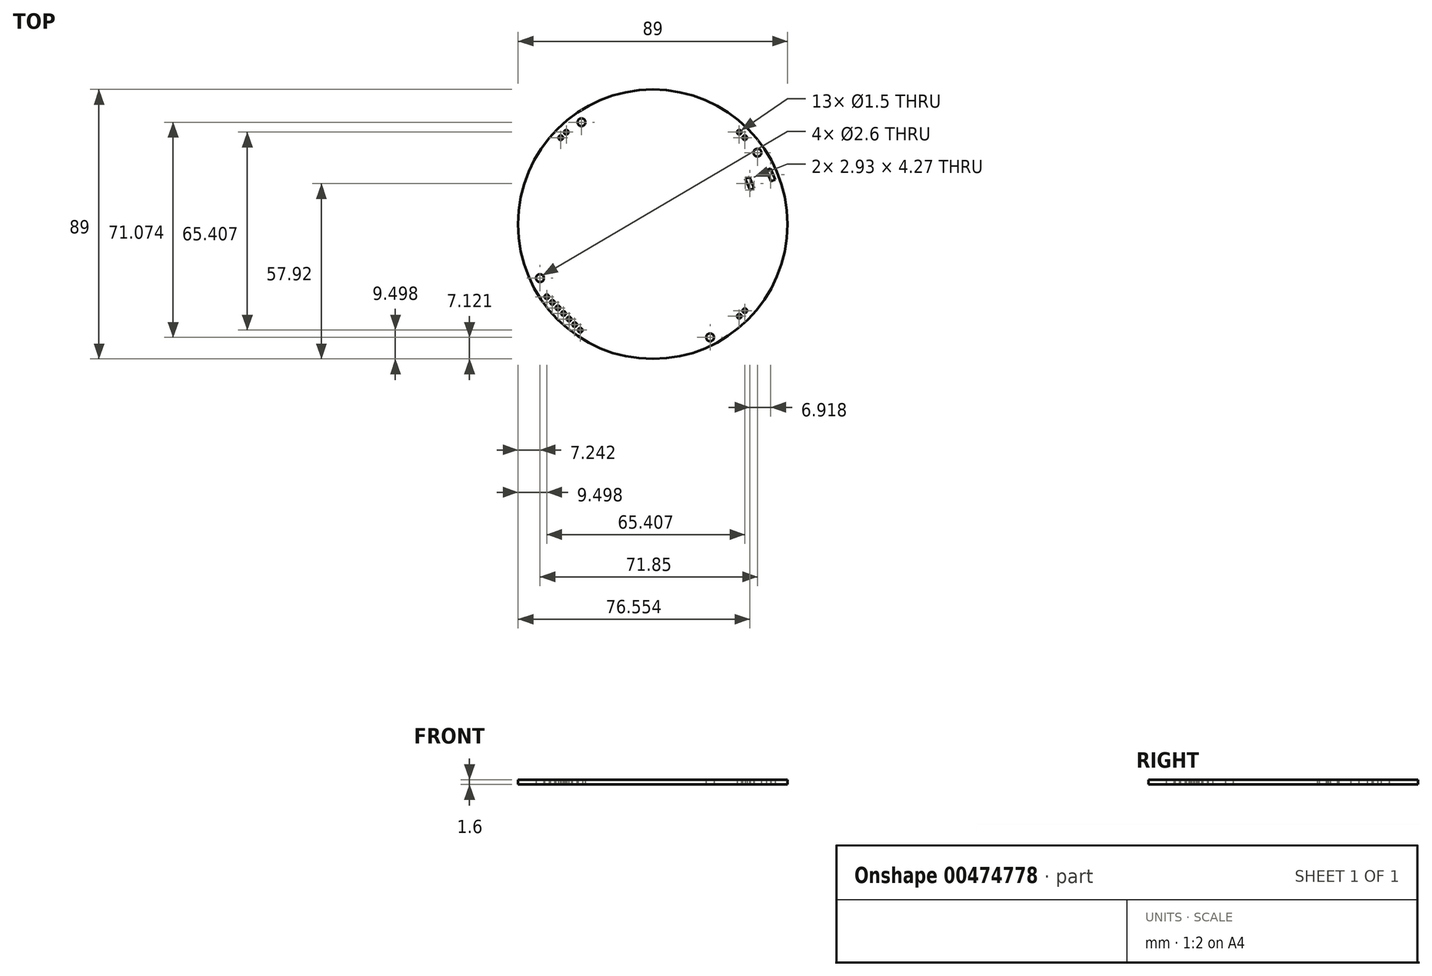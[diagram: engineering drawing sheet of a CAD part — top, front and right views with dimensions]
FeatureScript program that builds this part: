
annotation { "Feature Type Name" : "Feature", "Feature Type Description" : "" }
export const myFeature = defineFeature(function(context is Context, id is Id, definition is map)
    precondition{}
    {
        {
            var Q0;
            Q0=qCreatedBy(makeId("Top.planeOp"),FACE);
            var sketch = newSketch(context, id + "F0", { "sketchPlane" : qUnion([Q0])});
            skCircle(sketch, "E0", {"center": v(0, 0) * mm, "radius": 44.5 * mm});
            skLineSegment(sketch, "E1", {"start": v(-31.47, 31.47) * mm, "end": v(31.47, -31.47) * mm, "construction": true});
            skLineSegment(sketch, "E2", {"start": v(-31.47, -31.47) * mm, "end": v(31.47, 31.47) * mm, "construction": true});
            skLineSegment(sketch, "E3", {"start": v(-32.24, 28.57) * mm, "end": v(-30.4, 26.73) * mm, "construction": true});
            skLineSegment(sketch, "E4", {"start": v(-30.4, 26.73) * mm, "end": v(-26.73, 30.4) * mm, "construction": true});
            skLineSegment(sketch, "E5", {"start": v(-26.73, 30.4) * mm, "end": v(-28.57, 32.24) * mm, "construction": true});
            skLineSegment(sketch, "E6", {"start": v(-28.57, 32.24) * mm, "end": v(-32.24, 28.57) * mm, "construction": true});
            skLineSegment(sketch, "E7", {"start": v(28.57, 32.24) * mm, "end": v(32.24, 28.57) * mm, "construction": true});
            skLineSegment(sketch, "E8", {"start": v(32.24, 28.57) * mm, "end": v(30.4, 26.73) * mm, "construction": true});
            skLineSegment(sketch, "E9", {"start": v(30.4, 26.73) * mm, "end": v(26.73, 30.4) * mm, "construction": true});
            skLineSegment(sketch, "E10", {"start": v(26.73, 30.4) * mm, "end": v(28.57, 32.24) * mm, "construction": true});
            skLineSegment(sketch, "E11", {"start": v(28.57, -32.24) * mm, "end": v(26.73, -30.4) * mm, "construction": true});
            skLineSegment(sketch, "E12", {"start": v(26.73, -30.4) * mm, "end": v(30.4, -26.73) * mm, "construction": true});
            skLineSegment(sketch, "E13", {"start": v(30.4, -26.73) * mm, "end": v(32.24, -28.57) * mm, "construction": true});
            skLineSegment(sketch, "E14", {"start": v(32.24, -28.57) * mm, "end": v(28.57, -32.24) * mm, "construction": true});
            skLineSegment(sketch, "E15", {"start": v(-36.84, -23.97) * mm, "end": v(-35, -22.13) * mm, "construction": true});
            skLineSegment(sketch, "E16", {"start": v(-35, -22.13) * mm, "end": v(-22.13, -35) * mm, "construction": true});
            skLineSegment(sketch, "E17", {"start": v(-22.13, -35) * mm, "end": v(-23.97, -36.84) * mm, "construction": true});
            skLineSegment(sketch, "E18", {"start": v(-23.97, -36.84) * mm, "end": v(-36.84, -23.97) * mm, "construction": true});
            skCircle(sketch, "E19", {"center": v(-30.4, 28.57) * mm, "radius": 0.75 * mm});
            skCircle(sketch, "E20", {"center": v(-28.57, 30.4) * mm, "radius": 0.75 * mm});
            skCircle(sketch, "E21", {"center": v(28.57, 30.4) * mm, "radius": 0.75 * mm});
            skCircle(sketch, "E22", {"center": v(30.4, 28.57) * mm, "radius": 0.75 * mm});
            skCircle(sketch, "E23", {"center": v(30.4, -28.57) * mm, "radius": 0.75 * mm});
            skCircle(sketch, "E24", {"center": v(28.57, -30.4) * mm, "radius": 0.75 * mm});
            skCircle(sketch, "E25", {"center": v(-29.49, -29.49) * mm, "radius": 0.75 * mm});
            skCircle(sketch, "E26", {"center": v(-35, -23.97) * mm, "radius": 0.75 * mm});
            skCircle(sketch, "E27", {"center": v(-33.16, -25.8) * mm, "radius": 0.75 * mm});
            skCircle(sketch, "E28", {"center": v(-31.32, -27.65) * mm, "radius": 0.75 * mm});
            skCircle(sketch, "E29", {"center": v(-27.65, -31.32) * mm, "radius": 0.75 * mm});
            skCircle(sketch, "E30", {"center": v(-25.8, -33.16) * mm, "radius": 0.75 * mm});
            skCircle(sketch, "E31", {"center": v(-23.97, -35) * mm, "radius": 0.75 * mm});
            skLineSegment(sketch, "E32", {"start": v(-35.92, -23.05) * mm, "end": v(-23.05, -35.92) * mm, "construction": true});
            skLineSegment(sketch, "E33", {"start": v(27.65, -31.32) * mm, "end": v(31.32, -27.65) * mm, "construction": true});
            skLineSegment(sketch, "E34", {"start": v(27.65, 31.32) * mm, "end": v(31.32, 27.65) * mm, "construction": true});
            skLineSegment(sketch, "E35", {"start": v(-31.32, 27.65) * mm, "end": v(-27.65, 31.32) * mm, "construction": true});
            skLineSegment(sketch, "E36", {"start": v(-37.26, -17.81) * mm, "end": v(-23.55, 33.7) * mm, "construction": true});
            skLineSegment(sketch, "E37", {"start": v(-23.55, 33.7) * mm, "end": v(34.6, 23.64) * mm, "construction": true});
            skLineSegment(sketch, "E38", {"start": v(34.6, 23.64) * mm, "end": v(18.93, -37.38) * mm, "construction": true});
            skLineSegment(sketch, "E39", {"start": v(18.93, -37.38) * mm, "end": v(-37.26, -17.81) * mm, "construction": true});
            skLineSegment(sketch, "E40", {"start": v(-23.55, 33.7) * mm, "end": v(18.93, -37.38) * mm, "construction": true});
            skCircle(sketch, "E41", {"center": v(-37.26, -17.81) * mm, "radius": 1.3 * mm});
            skCircle(sketch, "E42", {"center": v(18.93, -37.38) * mm, "radius": 1.3 * mm});
            skCircle(sketch, "E43", {"center": v(34.6, 23.64) * mm, "radius": 1.3 * mm});
            skCircle(sketch, "E44", {"center": v(-23.55, 33.7) * mm, "radius": 1.3 * mm});
            skLineSegment(sketch, "E45", {"start": v(0, 0) * mm, "end": v(41.05, 17.19) * mm, "construction": true});
            skLineSegment(sketch, "E46", {"start": v(29.64, 17.24) * mm, "end": v(33.08, 9.03) * mm, "construction": true});
            skLineSegment(sketch, "E47", {"start": v(33.08, 9.03) * mm, "end": v(46, 14.43) * mm, "construction": true});
            skLineSegment(sketch, "E48", {"start": v(46, 14.43) * mm, "end": v(42.56, 22.64) * mm, "construction": true});
            skLineSegment(sketch, "E49", {"start": v(42.56, 22.64) * mm, "end": v(29.64, 17.24) * mm, "construction": true});
            skLineSegment(sketch, "E50", {"start": v(32.13, 11.29) * mm, "end": v(30.59, 14.98) * mm});
            skLineSegment(sketch, "E51", {"start": v(30.59, 14.98) * mm, "end": v(31.97, 15.55) * mm});
            skLineSegment(sketch, "E52", {"start": v(31.97, 15.55) * mm, "end": v(33.52, 11.87) * mm});
            skLineSegment(sketch, "E53", {"start": v(33.52, 11.87) * mm, "end": v(32.13, 11.29) * mm});
            skLineSegment(sketch, "E54", {"start": v(39.05, 14.18) * mm, "end": v(37.5, 17.87) * mm});
            skLineSegment(sketch, "E55", {"start": v(37.5, 17.87) * mm, "end": v(38.9, 18.45) * mm});
            skLineSegment(sketch, "E56", {"start": v(38.9, 18.45) * mm, "end": v(40.44, 14.76) * mm});
            skLineSegment(sketch, "E57", {"start": v(40.44, 14.76) * mm, "end": v(39.05, 14.18) * mm});
            skSolve(sketch);
        }
        {
            var Q0;
            Q0 = qSketchRegion(id + "F0", true);
            extrude(context, id + "F1", {"entities" : qUnion([Q0]), "depth" : 1.6 * mm});
        }
    });
